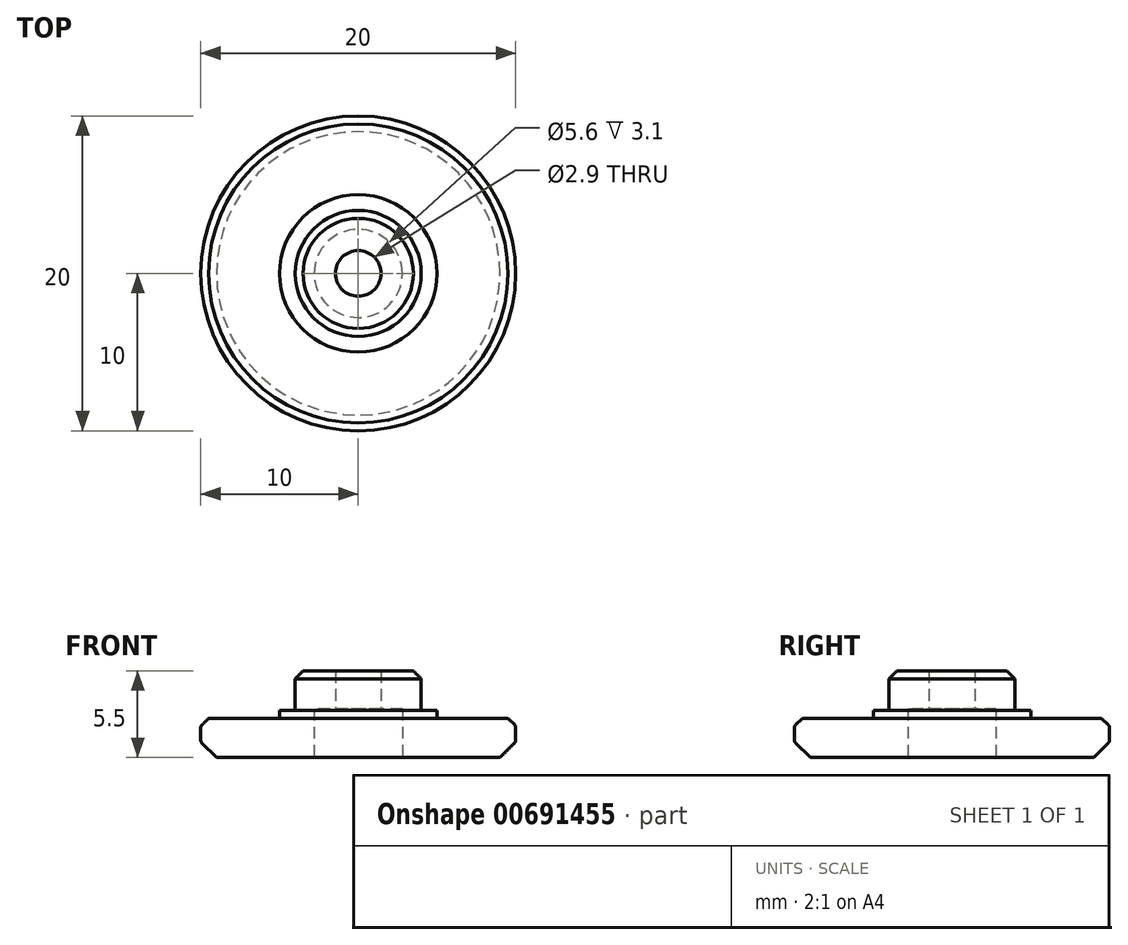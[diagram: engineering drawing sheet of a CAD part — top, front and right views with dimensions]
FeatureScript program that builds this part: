
annotation { "Feature Type Name" : "Feature", "Feature Type Description" : "" }
export const myFeature = defineFeature(function(context is Context, id is Id, definition is map)
    precondition{}
    {
        {
            var Q0;
            Q0=qCreatedBy(makeId("Top.planeOp"),FACE);
            var sketch = newSketch(context, id + "F0", { "sketchPlane" : qUnion([Q0])});
            skCircle(sketch, "E0", {"center": v(0, 0) * mm, "radius": 4 * mm});
            skSolve(sketch);
        }
        {
            var Q0;
            Q0=makeQuery(id+"F0.imprint","IMPRINT",FACE,{"disambiguationData":[TD([[makeQuery(id+"F0.imprint","IMPRINT",EDGE,{"derivedFrom":sQuery(id+"F0.wireOp",EDGE,"E0")}),1.0]])]});
            extrude(context, id + "F1", {"entities" : qUnion([Q0]), "depth" : 5.5 * mm, "offsetDistance" : 25 * mm});
        }
        {
            var Q0;
            Q0=qCreatedBy(makeId("Top.planeOp"),FACE);
            var sketch = newSketch(context, id + "F2", { "sketchPlane" : qUnion([Q0])});
            skCircle(sketch, "E1", {"center": v(0, 0) * mm, "radius": 5 * mm});
            skSolve(sketch);
        }
        {
            var Q0;
            Q0=makeQuery(id+"F2.imprint","IMPRINT",FACE,{"disambiguationData":[TD([[makeQuery(id+"F2.imprint","IMPRINT",EDGE,{"derivedFrom":sQuery(id+"F2.wireOp",EDGE,"E1")}),1.0]])]});
            extrude(context, id + "F3", {"entities" : qUnion([Q0]), "operationType" : NewBodyOperationType.ADD, "depth" : 3 * mm, "offsetDistance" : 25 * mm});
        }
        {
            var Q0;
            Q0=qCreatedBy(makeId("Top.planeOp"),FACE);
            var sketch = newSketch(context, id + "F4", { "sketchPlane" : qUnion([Q0])});
            skCircle(sketch, "E2", {"center": v(0, 0) * mm, "radius": 10 * mm});
            skSolve(sketch);
        }
        {
            var Q0;
            Q0 = qSketchRegion(id + "F4", true);
            extrude(context, id + "F5", {"entities" : qUnion([Q0]), "operationType" : NewBodyOperationType.ADD, "depth" : 2.5 * mm, "offsetDistance" : 25 * mm});
        }
        {
            var Q0;
            Q0=makeQuery(id+"F5.opExtrude","CAP_EDGE",EDGE,{"disambiguationData":[OSD([sQuery(id+"F4.wireOp",EDGE,"E2")])],"isStart":true});
            chamfer(context, id + "F6", {"entities" : qUnion([Q0]), "width" : 1 * mm, "tangentPropagation" : true});
        }
        {
            var Q0;
            Q0=makeQuery(id+"F5.opExtrude","CAP_EDGE",EDGE,{"disambiguationData":[OSD([sQuery(id+"F4.wireOp",EDGE,"E2")])],"isStart":false});
            chamfer(context, id + "F7", {"entities" : qUnion([Q0]), "width" : .5 * mm, "tangentPropagation" : true});
        }
        {
            var Q0;
            {var subQ0=sQuery(id+"F4.wireOp",EDGE,"E2");Q0=makeQuery(id+"F6.opChamfer","BLEND_EDGE",EDGE,{"blendedFrom":[makeQuery(id+"F5.opExtrude","CAP_EDGE",EDGE,{"disambiguationData":[OSD([subQ0])],"isStart":true}),makeQuery(id+"F5.opExtrude","SWEPT_FACE",FACE,{"disambiguationData":[OSD([subQ0])]})],"blendedInto":[makeQuery(id+"F5.opExtrude","SWEPT_FACE",FACE,{"disambiguationData":[OSD([subQ0])]})]});}
            var Q1;
            {var subQ0=sQuery(id+"F4.wireOp",EDGE,"E2");Q1=makeQuery(id+"F7.opChamfer","BLEND_EDGE",EDGE,{"blendedFrom":[makeQuery(id+"F5.opExtrude","CAP_EDGE",EDGE,{"disambiguationData":[OSD([subQ0])],"isStart":false}),makeQuery(id+"F5.opExtrude","SWEPT_FACE",FACE,{"disambiguationData":[OSD([subQ0])]})],"blendedInto":[makeQuery(id+"F5.opExtrude","SWEPT_FACE",FACE,{"disambiguationData":[OSD([subQ0])]})]});}
            fillet(context, id + "F8", {"entities" : qUnion([Q0, Q1]), "radius" : .2 * mm, "tangentPropagation" : true, "allowEdgeOverflow" : false});
        }
        {
            var Q0;
            Q0=makeQuery(id+"F1.opExtrude","CAP_EDGE",EDGE,{"disambiguationData":[OSD([sQuery(id+"F0.wireOp",EDGE,"E0")])],"isStart":false});
            chamfer(context, id + "F9", {"entities" : qUnion([Q0]), "width" : .5 * mm, "tangentPropagation" : true});
        }
        {
            var Q0;
            Q0=makeQuery(id+"F1.opExtrude","SWEPT_BODY",BODY,{"disambiguationData":[OSD([sQuery(id+"F0.wireOp",EDGE,"E0")])]});
            transform(context, id + "F10", {"entities" : qUnion([Q0]), "transformType" : TransformType.TRANSLATION_3D, "dx" : -25 * mm, "dy" : 0 * mm, "dz" : 0 * mm, "makeCopy" : true});
        }
        {
            var Q0;
            Q0=qCreatedBy(makeId("Top.planeOp"),FACE);
            var sketch = newSketch(context, id + "F11", { "sketchPlane" : qUnion([Q0])});
            skCircle(sketch, "E3", {"center": v(0, 0) * mm, "radius": 2.8 * mm});
            skSolve(sketch);
        }
        {
            var Q0;
            Q0=makeQuery(id+"F11.imprint","IMPRINT",FACE,{"disambiguationData":[TD([[makeQuery(id+"F11.imprint","IMPRINT",EDGE,{"derivedFrom":sQuery(id+"F11.wireOp",EDGE,"E3")}),1.0]])]});
            var Q1;
            Q1=sQuery(id+"F11.wireOp",EDGE,"E3");
            extrude(context, id + "F12", {"entities" : qUnion([Q0]), "operationType" : NewBodyOperationType.REMOVE, "surfaceEntities" : qUnion([Q1]), "depth" : 3.1 * mm, "offsetDistance" : 25 * mm});
        }
        {
            var Q0;
            Q0=qCreatedBy(makeId("Top.planeOp"),FACE);
            var sketch = newSketch(context, id + "F13", { "sketchPlane" : qUnion([Q0])});
            skCircle(sketch, "E4", {"center": v(0, 0) * mm, "radius": 1.45 * mm});
            skSolve(sketch);
        }
        {
            var Q0;
            Q0=makeQuery(id+"F13.imprint","IMPRINT",FACE,{"disambiguationData":[TD([[makeQuery(id+"F13.imprint","IMPRINT",EDGE,{"derivedFrom":sQuery(id+"F13.wireOp",EDGE,"E4")}),1.0]])]});
            var Q1;
            Q1=sQuery(id+"F13.wireOp",EDGE,"E4");
            extrude(context, id + "F14", {"entities" : qUnion([Q0]), "operationType" : NewBodyOperationType.REMOVE, "surfaceEntities" : qUnion([Q1]), "depth" : 8.4 * mm, "offsetDistance" : 25 * mm});
        }
        {
            var Q0;
            Q0=makeQuery(id+"F10.opPattern","COPY",BODY,{"derivedFrom":makeQuery(id+"F1.opExtrude","SWEPT_BODY",BODY,{"disambiguationData":[OSD([sQuery(id+"F0.wireOp",EDGE,"E0")])]}),"instanceName":"1"});
            deleteBodies(context, id + "F15", {"entities" : qUnion([Q0])});
        }
        {
            var Q0;
            Q0=makeQuery(id+"F1.opExtrude","SWEPT_BODY",BODY,{"disambiguationData":[OSD([sQuery(id+"F0.wireOp",EDGE,"E0")])]});
            transform(context, id + "F16", {"entities" : qUnion([Q0]), "transformType" : TransformType.TRANSLATION_3D, "dx" : -23.4 * mm, "dy" : 0 * mm, "dz" : 0 * mm, "makeCopy" : true});
        }
        {
            var Q0;
            Q0=makeQuery(id+"F16.opPattern","COPY",BODY,{"derivedFrom":makeQuery(id+"F1.opExtrude","SWEPT_BODY",BODY,{"disambiguationData":[OSD([sQuery(id+"F0.wireOp",EDGE,"E0")])]}),"instanceName":"1"});
            deleteBodies(context, id + "F17", {"entities" : qUnion([Q0])});
        }
    });
